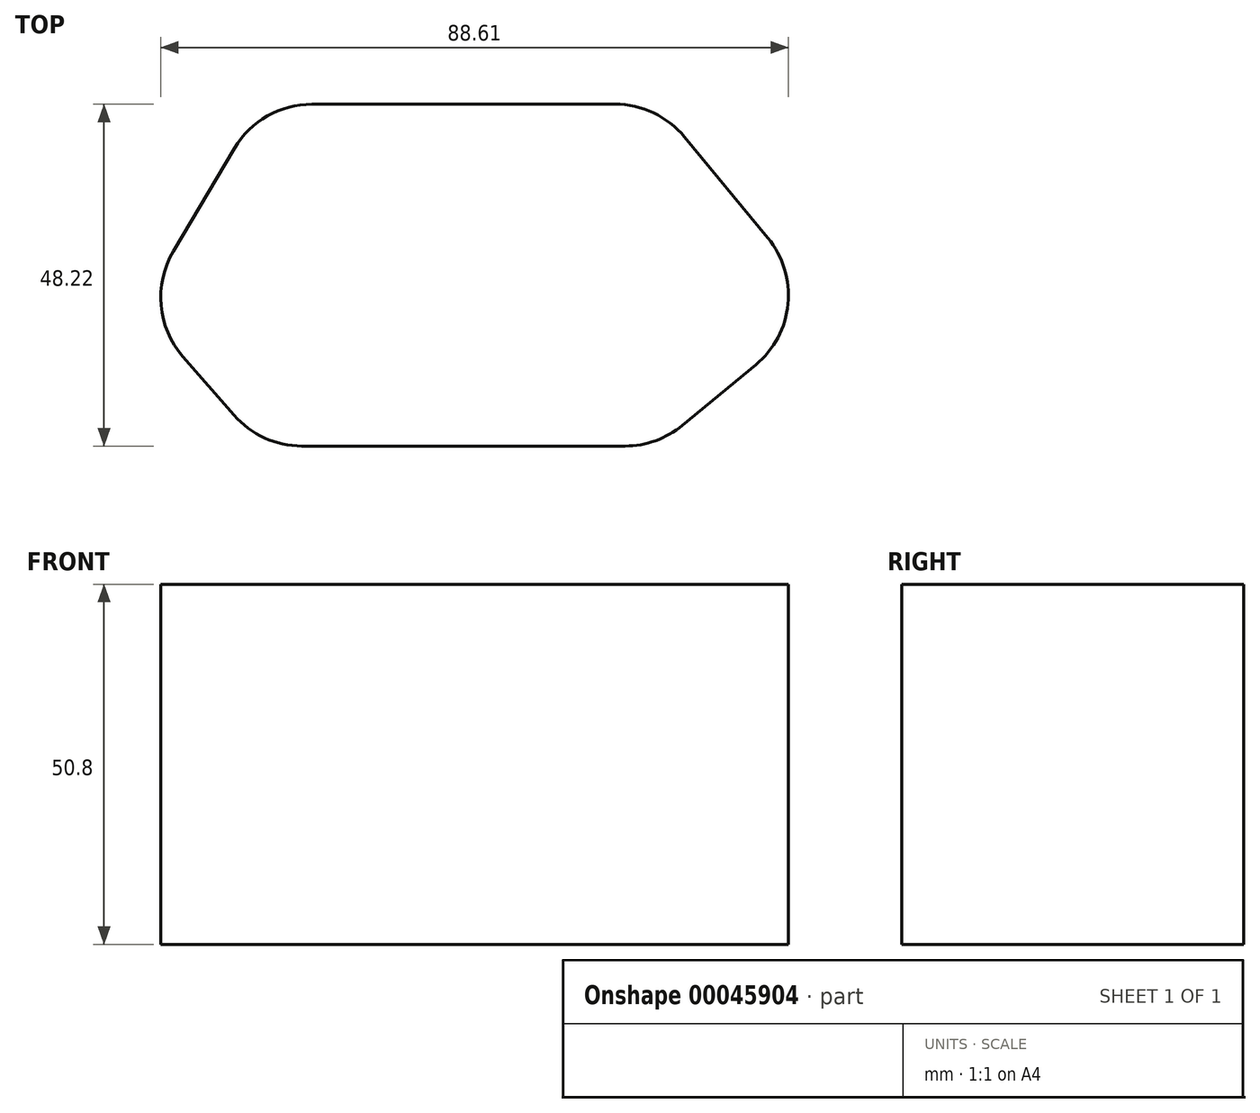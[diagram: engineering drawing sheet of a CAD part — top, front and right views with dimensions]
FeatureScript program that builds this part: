
annotation { "Feature Type Name" : "Feature", "Feature Type Description" : "" }
export const myFeature = defineFeature(function(context is Context, id is Id, definition is map)
    precondition{}
    {
        {
            var Q0;
            Q0=qCreatedBy(makeId("Top.planeOp"),FACE);
            var sketch = newSketch(context, id + "F0", { "sketchPlane" : qUnion([Q0])});
            skLineSegment(sketch, "E0", {"start": v(-43.22, 7.9) * mm, "end": v(-34.57, 22.46) * mm});
            skLineSegment(sketch, "E1", {"start": v(-23.66, 28.67) * mm, "end": v(19.12, 28.67) * mm});
            skLineSegment(sketch, "E2", {"start": v(28.91, 24.05) * mm, "end": v(40.7, 9.8) * mm});
            skLineSegment(sketch, "E3", {"start": v(38.99, -8.09) * mm, "end": v(28.62, -16.64) * mm});
            skLineSegment(sketch, "E4", {"start": v(20.54, -19.55) * mm, "end": v(-25.1, -19.55) * mm});
            skLineSegment(sketch, "E5", {"start": v(-34.68, -15.2) * mm, "end": v(-41.88, -6.93) * mm});
            skPoint(sketch, "E6.visualSharp", {"position": v(-30.88, 28.67) * mm});
            skArc(sketch, "E6.filletArc", {"start": v(-23.66, 28.67) * mm, "mid": v(-29.94, 27) * mm, "end": v(-34.57, 22.46) * mm});
            skPoint(sketch, "E7.visualSharp", {"position": v(25.1, 28.67) * mm});
            skArc(sketch, "E7.filletArc", {"start": v(28.91, 24.05) * mm, "mid": v(24.53, 27.46) * mm, "end": v(19.12, 28.67) * mm});
            skPoint(sketch, "E8.visualSharp", {"position": v(48.78, 0) * mm});
            skArc(sketch, "E8.filletArc", {"start": v(38.99, -8.09) * mm, "mid": v(43.54, 0.5) * mm, "end": v(40.7, 9.8) * mm});
            skPoint(sketch, "E9.visualSharp", {"position": v(25.1, -19.55) * mm});
            skArc(sketch, "E9.filletArc", {"start": v(20.54, -19.55) * mm, "mid": v(24.83, -18.8) * mm, "end": v(28.62, -16.64) * mm});
            skPoint(sketch, "E10.visualSharp", {"position": v(-30.88, -19.55) * mm});
            skArc(sketch, "E10.filletArc", {"start": v(-34.68, -15.2) * mm, "mid": v(-30.36, -18.41) * mm, "end": v(-25.1, -19.55) * mm});
            skPoint(sketch, "E11.visualSharp", {"position": v(-47.92, 0) * mm});
            skArc(sketch, "E11.filletArc", {"start": v(-43.22, 7.9) * mm, "mid": v(-44.95, 0.27) * mm, "end": v(-41.88, -6.93) * mm});
            skSolve(sketch);
        }
        {
            var Q0;
            Q0 = qSketchRegion(id + "F0", true);
            extrude(context, id + "F1", {"entities" : qUnion([Q0]), "depth" : 50.8 * mm});
        }
    });
